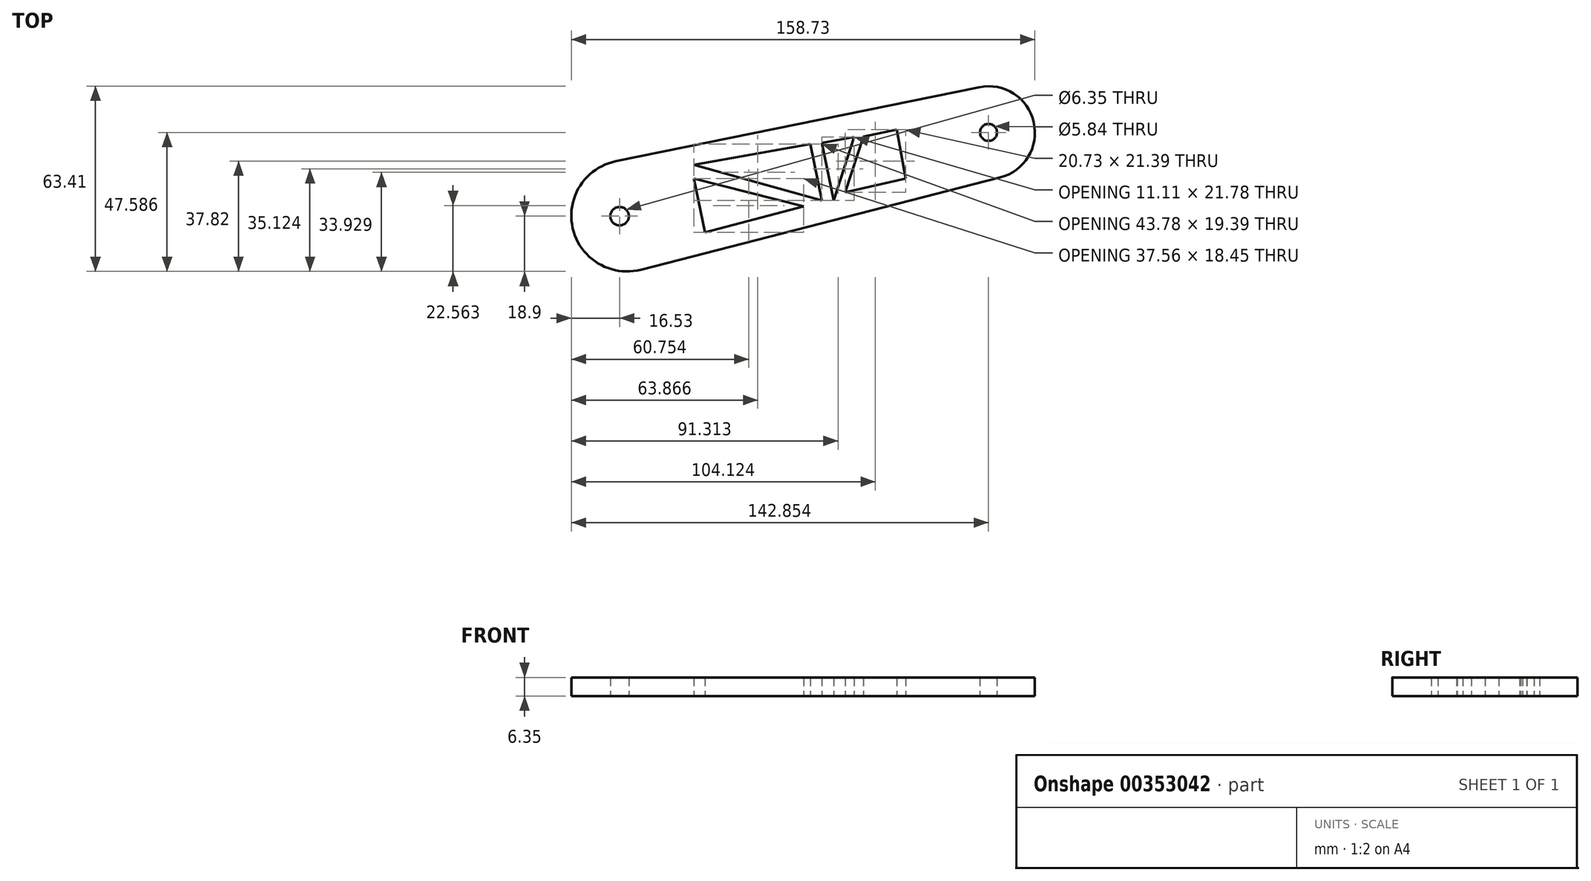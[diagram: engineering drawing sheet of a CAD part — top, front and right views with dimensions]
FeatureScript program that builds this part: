
annotation { "Feature Type Name" : "Feature", "Feature Type Description" : "" }
export const myFeature = defineFeature(function(context is Context, id is Id, definition is map)
    precondition{}
    {
        {
            var Q0;
            Q0=qCreatedBy(makeId("Top.planeOp"),FACE);
            var sketch = newSketch(context, id + "F0", { "sketchPlane" : qUnion([Q0])});
            skLineSegment(sketch, "E0", {"start": v(7.26, -18.3) * mm, "end": v(130.27, 13.26) * mm});
            skArc(sketch, "E1", {"start": v(130.27, 13.26) * mm, "mid": v(141.8, 32.2) * mm, "end": v(123.15, 44.2) * mm});
            skLineSegment(sketch, "E2", {"start": v(-1.28, 18.82) * mm, "end": v(123.15, 44.2) * mm});
            skCircle(sketch, "E3", {"center": v(0, 0) * mm, "radius": 3.18 * mm});
            skArc(sketch, "E4", {"start": v(-1.28, 18.82) * mm, "mid": v(-16.04, -4.12) * mm, "end": v(7.26, -18.3) * mm});
            skLineSegment(sketch, "E5", {"start": v(0, 0) * mm, "end": v(14, 0) * mm, "construction": true});
            skCircle(sketch, "E6", {"center": v(126.32, 28.69) * mm, "radius": 2.92 * mm});
            skLineSegment(sketch, "E7", {"start": v(25.44, 12.9) * mm, "end": v(29.2, -5.56) * mm});
            skLineSegment(sketch, "E8", {"start": v(29.2, -5.56) * mm, "end": v(25.44, 12.9) * mm});
            skLineSegment(sketch, "E9", {"start": v(63, 3.33) * mm, "end": v(25.44, 12.9) * mm});
            skLineSegment(sketch, "E10", {"start": v(29.2, -5.56) * mm, "end": v(63, 3.33) * mm});
            skLineSegment(sketch, "E11", {"start": v(25.44, 17.56) * mm, "end": v(69.23, 5.33) * mm});
            skLineSegment(sketch, "E12", {"start": v(69.23, 5.33) * mm, "end": v(65.27, 24.72) * mm});
            skLineSegment(sketch, "E13", {"start": v(65.27, 24.72) * mm, "end": v(25.44, 17.56) * mm});
            skLineSegment(sketch, "E14", {"start": v(69.23, 25.11) * mm, "end": v(73.26, 5.33) * mm});
            skLineSegment(sketch, "E15", {"start": v(73.26, 5.33) * mm, "end": v(80.34, 27.11) * mm});
            skLineSegment(sketch, "E16", {"start": v(80.34, 27.11) * mm, "end": v(69.23, 25.11) * mm});
            skLineSegment(sketch, "E17", {"start": v(77.23, 8.22) * mm, "end": v(83.42, 27.26) * mm});
            skLineSegment(sketch, "E18", {"start": v(83.42, 27.26) * mm, "end": v(94.95, 29.62) * mm});
            skLineSegment(sketch, "E19", {"start": v(94.95, 29.62) * mm, "end": v(97.96, 12.9) * mm});
            skLineSegment(sketch, "E20", {"start": v(97.96, 12.9) * mm, "end": v(77.23, 8.22) * mm});
            skSolve(sketch);
        }
        {
            var Q0;
            Q0=makeQuery(id+"F0.imprint","IMPRINT",FACE,{"disambiguationData":[TD([[makeQuery(id+"F0.imprint","IMPRINT",EDGE,{"derivedFrom":sQuery(id+"F0.wireOp",EDGE,"E0")}),1.0]])]});
            extrude(context, id + "F1", {"entities" : qUnion([Q0]), "depth" : 6.35 * mm});
        }
    });
